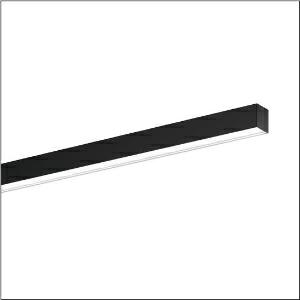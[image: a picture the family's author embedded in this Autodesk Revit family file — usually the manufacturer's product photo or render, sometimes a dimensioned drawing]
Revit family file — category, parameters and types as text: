
# Revit family: silica_r__21_51mx23dc4abb_ae3b
name_source: partatom
category: Lighting Fixtures
units: mm (PartAtom-declared; Revit-internal decimal feet)

## family parameters
Cut with Voids When Loaded = No
Host = Face
Light Source = No
Part Type = Normal
Room Calculation Point = No
Round Connector Dimension = Use Diameter
Shared = No

## types (1)
- --- (1 x LED, 8200 lm, 58.2 W, 4000K)
    Apparent Load = 58 VA
    CIE Flux Codes = 78 96 99 100 100
    Color Rendering = 80
    Color Temperature = 4000K
    Default Elevation = 1800 mm
    Description = Silica® 21, office luminaire, primary optical cover: prismatic diffuser, of PMMA, CAT 2 (L<= 3000cd/m²), light emission: direct distribution, primary light characteristic: symmetric, installation type: surface-mounted, LED, rated luminous flux: 8.200lm, luminous efficacy: 141lm/W, light colour: 840, colour temperature: 4000K, with terminal, 3+2-pole, max. 2.5mm², mains connection: 220..240V, AC, 50/60Hz, rated input power: 58.2W, luminaire housing, of aluminium, jet black (RAL 9005), length: 3.004mm, width: 53mm, height: 53mm, protection rating (complete): IP20, insulation class (complete): insulation class I (protective earthing), certification: CE, permissible operating ambient temperature: 0..+35°C, standard: EN 50419, packaging unit: 1 piece
    Height = 0 mm  [stored 0 ft]
    Lamp = 1 x LED
    Lamp Light Flux = 8200 lm
    Lamp Power = 58.2 W
    Lamp count = 1
    Length = 3004 mm
    Luminous efficacy = 141 lm/W
    Manufacturer = Siteco
    ModVariant = No
    Model = 51MX23DC4ABB
    Mounting Place = Ceiling
    Mounting Type = Recessed
    Number of Poles = 1
    OnlyDefault = Yes
    Power Factor = 1
    Product Name = Silica® 21
    Product group = office luminaire | ceiling recessed
    ProductGroupID = 400
    Protection Class = Protection class I
    Protection Degree = IP 20
    RLX_Detail_Level = 1
    RLX_Emergency_Light_Flux = 0 lm
    RLX_Emergency_Type = 0
    RLX_Emergency_Type_DB = No
    RlxData = <blob elided: 23645 chars, md5=923ff502>
    Socket = socket
    Standby Power = 0 W
    System Light Flux = 8200 lm
    System Power = 58 W
    Type Comments = factory setting: luminous flux: 100 % | dim-lin: 254 | 323 mA
    Type Image = l_1335925.jpg
    URL = http://relux.com
    VarID = @adj_088673
    Voltage = 0 V
    Weight = 0.00 kg
    Width = 53 mm

note: [stored X ft] marks values corroborated as IEEE doubles in the binary element streams (Revit-internal decimal feet)

## geometry (parser evidence)
native form markers: Blend x4, Sweep x12
no freeform markers — native parametric forms only
